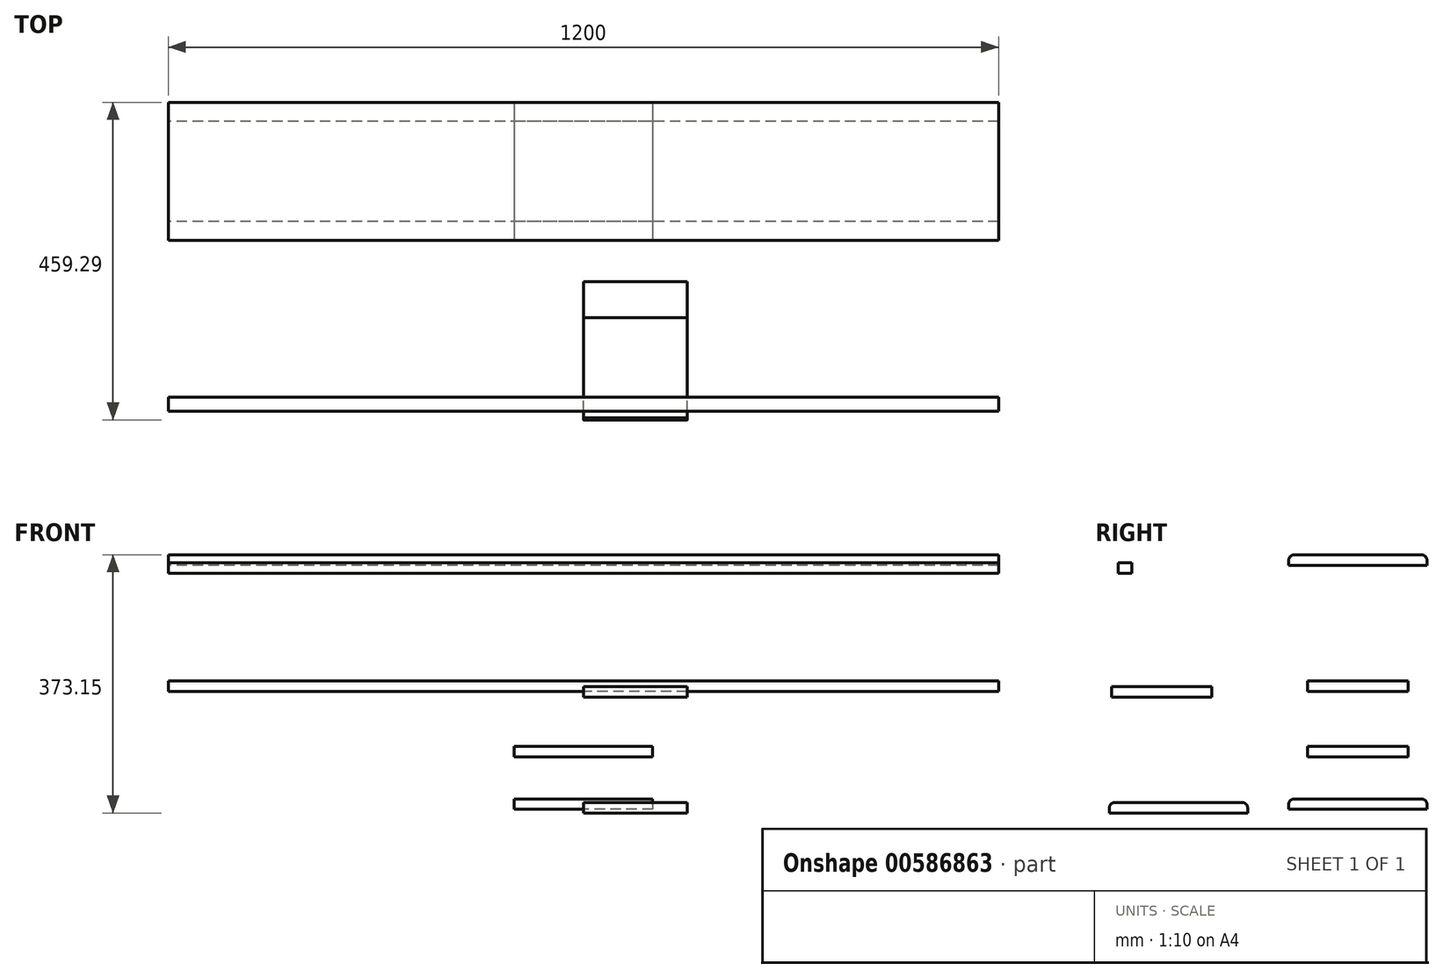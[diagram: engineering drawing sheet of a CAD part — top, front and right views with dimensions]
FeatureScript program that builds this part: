
annotation { "Feature Type Name" : "Feature", "Feature Type Description" : "" }
export const myFeature = defineFeature(function(context is Context, id is Id, definition is map)
    precondition{}
    {
        {
            var Q0;
            Q0=qCreatedBy(makeId("Right.planeOp"),FACE);
            var sketch = newSketch(context, id + "F0", { "sketchPlane" : qUnion([Q0])});
            skLineSegment(sketch, "E0.bottom", {"start": v(100, 172.95) * mm, "end": v(-100, 172.95) * mm});
            skLineSegment(sketch, "E0.top", {"start": v(100, 157.95) * mm, "end": v(-100, 157.95) * mm});
            skLineSegment(sketch, "E0.left", {"start": v(100, 172.95) * mm, "end": v(100, 157.95) * mm});
            skLineSegment(sketch, "E0.right", {"start": v(-100, 172.95) * mm, "end": v(-100, 157.95) * mm});
            skPoint(sketch, "E0.middle", {"position": v(0, 165.45) * mm});
            skSolve(sketch);
        }
        {
            var Q0;
            Q0=makeQuery(id+"F0.imprint","IMPRINT",FACE,{"disambiguationData":[TD([[makeQuery(id+"F0.imprint","IMPRINT",EDGE,{"derivedFrom":sQuery(id+"F0.wireOp",EDGE,"E0.bottom")}),1.0]])]});
            extrude(context, id + "F1", {"entities" : qUnion([Q0]), "endBound" : BoundingType.SYMMETRIC, "depth" : 1200 * mm, "offsetDistance" : 25 * mm});
        }
        {
            var Q0;
            Q0=makeQuery(id+"F1.opExtrude","SWEPT_EDGE",EDGE,{"disambiguationData":[OSD([sQuery(id+"F0.wireOp",EDGE,"E0.bottom"),sQuery(id+"F0.wireOp",EDGE,"E0.right")])]});
            var Q1;
            Q1=makeQuery(id+"F1.opExtrude","SWEPT_EDGE",EDGE,{"disambiguationData":[OSD([sQuery(id+"F0.wireOp",EDGE,"E0.bottom"),sQuery(id+"F0.wireOp",EDGE,"E0.left")])]});
            fillet(context, id + "F2", {"entities" : qUnion([Q0, Q1]), "radius" : 8 * mm, "tangentPropagation" : true, "allowEdgeOverflow" : false});
        }
        {
            var Q0;
            Q0=qCreatedBy(makeId("Right.planeOp"),FACE);
            var sketch = newSketch(context, id + "F3", { "sketchPlane" : qUnion([Q0])});
            skLineSegment(sketch, "E1.bottom", {"start": v(72.5, -24.5) * mm, "end": v(-72.5, -24.5) * mm});
            skLineSegment(sketch, "E1.top", {"start": v(72.5, -9.5) * mm, "end": v(-72.5, -9.5) * mm});
            skLineSegment(sketch, "E1.left", {"start": v(72.5, -24.5) * mm, "end": v(72.5, -9.5) * mm});
            skLineSegment(sketch, "E1.right", {"start": v(-72.5, -24.5) * mm, "end": v(-72.5, -9.5) * mm});
            skPoint(sketch, "E1.middle", {"position": v(0, -17) * mm});
            skSolve(sketch);
        }
        {
            var Q0;
            Q0=makeQuery(id+"F3.imprint","IMPRINT",FACE,{"disambiguationData":[TD([[makeQuery(id+"F3.imprint","IMPRINT",EDGE,{"derivedFrom":sQuery(id+"F3.wireOp",EDGE,"E1.bottom")}),-1.0]])]});
            extrude(context, id + "F4", {"entities" : qUnion([Q0]), "endBound" : BoundingType.SYMMETRIC, "depth" : 1200 * mm, "offsetDistance" : 25 * mm});
        }
        {
            var Q0;
            Q0=qCreatedBy(makeId("Right.planeOp"),FACE);
            var sketch = newSketch(context, id + "F5", { "sketchPlane" : qUnion([Q0])});
            skLineSegment(sketch, "E2.bottom", {"start": v(72.5, -104.05) * mm, "end": v(-72.5, -104.05) * mm});
            skLineSegment(sketch, "E2.top", {"start": v(72.5, -119.05) * mm, "end": v(-72.5, -119.05) * mm});
            skLineSegment(sketch, "E2.left", {"start": v(72.5, -104.05) * mm, "end": v(72.5, -119.05) * mm});
            skLineSegment(sketch, "E2.right", {"start": v(-72.5, -104.05) * mm, "end": v(-72.5, -119.05) * mm});
            skPoint(sketch, "E2.middle", {"position": v(0, -111.55) * mm});
            skLineSegment(sketch, "E3.bottom", {"start": v(92, -179.92) * mm, "end": v(-92, -179.92) * mm});
            skLineSegment(sketch, "E3.top", {"start": v(100, -194.92) * mm, "end": v(-100, -194.92) * mm});
            skLineSegment(sketch, "E3.left", {"start": v(100, -187.92) * mm, "end": v(100, -194.92) * mm});
            skLineSegment(sketch, "E3.right", {"start": v(-100, -187.92) * mm, "end": v(-100, -194.92) * mm});
            skPoint(sketch, "E3.middle", {"position": v(0, -187.42) * mm});
            skArc(sketch, "E4", {"start": v(-92, -179.92) * mm, "mid": v(-97.66, -182.26) * mm, "end": v(-100, -187.92) * mm});
            skArc(sketch, "E5", {"start": v(100, -187.92) * mm, "mid": v(97.66, -182.26) * mm, "end": v(92, -179.92) * mm});
            skPoint(sketch, "E6.orphan", {"position": v(-100, -179.92) * mm});
            skPoint(sketch, "E7.orphan", {"position": v(100, -179.92) * mm});
            skSolve(sketch);
        }
        {
            var Q0;
            Q0=makeQuery(id+"F5.imprint","IMPRINT",FACE,{"disambiguationData":[TD([[makeQuery(id+"F5.imprint","IMPRINT",EDGE,{"derivedFrom":sQuery(id+"F5.wireOp",EDGE,"E2.bottom")}),1.0]])]});
            var Q1;
            Q1=makeQuery(id+"F5.imprint","IMPRINT",FACE,{"disambiguationData":[TD([[makeQuery(id+"F5.imprint","IMPRINT",EDGE,{"derivedFrom":sQuery(id+"F5.wireOp",EDGE,"E3.bottom")}),1.0]])]});
            extrude(context, id + "F6", {"entities" : qUnion([Q0, Q1]), "endBound" : BoundingType.SYMMETRIC, "depth" : 200 * mm, "offsetDistance" : 25 * mm});
        }
        {
            var Q0;
            Q0=qCreatedBy(makeId("Right.planeOp"),FACE);
            var sketch = newSketch(context, id + "F7", { "sketchPlane" : qUnion([Q0])});
            skLineSegment(sketch, "E8.bottom", {"start": v(-356.15, -17.88) * mm, "end": v(-211.15, -17.88) * mm});
            skLineSegment(sketch, "E8.top", {"start": v(-356.15, -32.88) * mm, "end": v(-211.15, -32.88) * mm});
            skLineSegment(sketch, "E8.left", {"start": v(-356.15, -17.88) * mm, "end": v(-356.15, -32.88) * mm});
            skLineSegment(sketch, "E8.right", {"start": v(-211.15, -17.88) * mm, "end": v(-211.15, -32.88) * mm});
            skLineSegment(sketch, "E9.bottom", {"start": v(-359.3, -200.2) * mm, "end": v(-159.3, -200.2) * mm});
            skLineSegment(sketch, "E9.top", {"start": v(-351.3, -185.2) * mm, "end": v(-167.3, -185.2) * mm});
            skLineSegment(sketch, "E9.left", {"start": v(-359.3, -200.2) * mm, "end": v(-359.3, -193.2) * mm});
            skLineSegment(sketch, "E9.right", {"start": v(-159.3, -200.2) * mm, "end": v(-159.3, -193.2) * mm});
            skArc(sketch, "E10", {"start": v(-351.3, -185.2) * mm, "mid": v(-356.95, -187.54) * mm, "end": v(-359.3, -193.2) * mm});
            skArc(sketch, "E11", {"start": v(-159.3, -193.2) * mm, "mid": v(-161.63, -187.54) * mm, "end": v(-167.3, -185.2) * mm});
            skSolve(sketch);
        }
        {
            var Q0;
            Q0=makeQuery(id+"F7.imprint","IMPRINT",FACE,{"disambiguationData":[TD([[makeQuery(id+"F7.imprint","IMPRINT",EDGE,{"derivedFrom":sQuery(id+"F7.wireOp",EDGE,"E8.bottom")}),-1.0]])]});
            var Q1;
            Q1=makeQuery(id+"F7.imprint","IMPRINT",FACE,{"disambiguationData":[TD([[makeQuery(id+"F7.imprint","IMPRINT",EDGE,{"derivedFrom":sQuery(id+"F7.wireOp",EDGE,"E9.bottom")}),1.0]])]});
            extrude(context, id + "F8", {"entities" : qUnion([Q0, Q1]), "depth" : 150 * mm, "offsetDistance" : 25 * mm});
        }
        {
            var Q0;
            Q0=qCreatedBy(makeId("Right.planeOp"),FACE);
            var sketch = newSketch(context, id + "F9", { "sketchPlane" : qUnion([Q0])});
            skLineSegment(sketch, "E12.bottom", {"start": v(-326.63, 146.51) * mm, "end": v(-346.63, 146.51) * mm});
            skLineSegment(sketch, "E12.top", {"start": v(-326.63, 161.51) * mm, "end": v(-346.63, 161.51) * mm});
            skLineSegment(sketch, "E12.left", {"start": v(-326.63, 146.51) * mm, "end": v(-326.63, 161.51) * mm});
            skLineSegment(sketch, "E12.right", {"start": v(-346.63, 146.51) * mm, "end": v(-346.63, 161.51) * mm});
            skSolve(sketch);
        }
        {
            var Q0;
            Q0 = qSketchRegion(id + "F9", true);
            extrude(context, id + "F10", {"entities" : qUnion([Q0]), "endBound" : BoundingType.SYMMETRIC, "depth" : 1200 * mm, "offsetDistance" : 25 * mm});
        }
    });
